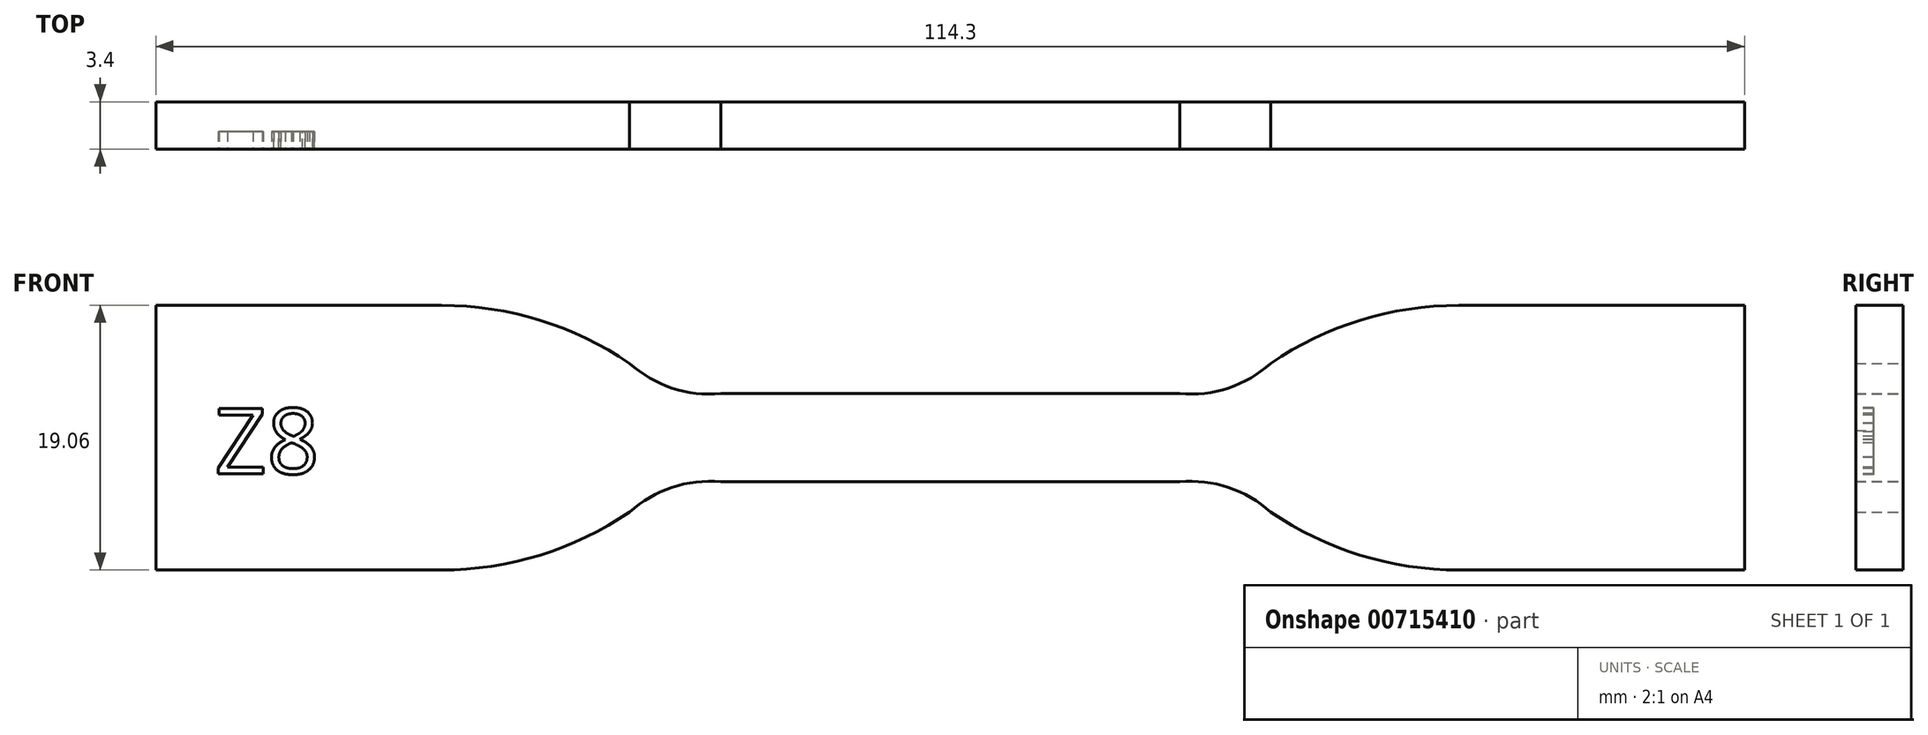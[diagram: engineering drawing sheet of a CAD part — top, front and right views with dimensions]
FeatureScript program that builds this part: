
annotation { "Feature Type Name" : "Feature", "Feature Type Description" : "" }
export const myFeature = defineFeature(function(context is Context, id is Id, definition is map)
    precondition{}
    {
        {
            var Q0;
            Q0=qCreatedBy(makeId("Front.planeOp"),FACE);
            var sketch = newSketch(context, id + "F0", { "sketchPlane" : qUnion([Q0])});
            skLineSegment(sketch, "E0", {"start": v(-57.15, 0) * mm, "end": v(-57.15, -9.52) * mm});
            skLineSegment(sketch, "E1", {"start": v(-57.15, -9.53) * mm, "end": v(-36.58, -9.53) * mm});
            skArc(sketch, "E2", {"start": v(-36.58, -9.53) * mm, "mid": v(-29.51, -8.46) * mm, "end": v(-23.07, -5.35) * mm});
            skArc(sketch, "E3", {"start": v(-16.51, -3.17) * mm, "mid": v(-20.02, -3.58) * mm, "end": v(-23.07, -5.35) * mm});
            skLineSegment(sketch, "E4", {"start": v(-16.51, -3.17) * mm, "end": v(0, -3.17) * mm});
            skArc(sketch, "E5.MirrorCS", {"start": v(-16.51, 3.17) * mm, "mid": v(-20.02, 3.58) * mm, "end": v(-23.07, 5.35) * mm});
            skLineSegment(sketch, "E6.MirrorCS", {"start": v(-16.51, 3.17) * mm, "end": v(0, 3.17) * mm});
            skArc(sketch, "E7.MirrorCS", {"start": v(-36.58, 9.53) * mm, "mid": v(-29.51, 8.46) * mm, "end": v(-23.07, 5.35) * mm});
            skLineSegment(sketch, "E8.MirrorCS", {"start": v(-57.15, 0) * mm, "end": v(-57.15, 9.52) * mm});
            skLineSegment(sketch, "E9.MirrorCS", {"start": v(-57.15, 9.53) * mm, "end": v(-36.58, 9.53) * mm});
            skArc(sketch, "E10.MirrorCS", {"start": v(36.58, -9.53) * mm, "mid": v(29.51, -8.46) * mm, "end": v(23.07, -5.35) * mm});
            skLineSegment(sketch, "E11.MirrorCS", {"start": v(57.15, 0) * mm, "end": v(57.15, -9.52) * mm});
            skArc(sketch, "E12.MirrorCS", {"start": v(16.51, -3.17) * mm, "mid": v(20.02, -3.58) * mm, "end": v(23.07, -5.35) * mm});
            skLineSegment(sketch, "E13.MirrorCS", {"start": v(16.51, 3.17) * mm, "end": v(0, 3.17) * mm});
            skLineSegment(sketch, "E14.MirrorCS", {"start": v(57.15, -9.53) * mm, "end": v(36.58, -9.53) * mm});
            skArc(sketch, "E15.MirrorCS", {"start": v(16.51, 3.17) * mm, "mid": v(20.02, 3.58) * mm, "end": v(23.07, 5.35) * mm});
            skArc(sketch, "E16.MirrorCS", {"start": v(36.58, 9.53) * mm, "mid": v(29.51, 8.46) * mm, "end": v(23.07, 5.35) * mm});
            skLineSegment(sketch, "E17.MirrorCS", {"start": v(57.15, 9.53) * mm, "end": v(36.58, 9.53) * mm});
            skLineSegment(sketch, "E18.MirrorCS", {"start": v(57.15, 0) * mm, "end": v(57.15, 9.52) * mm});
            skLineSegment(sketch, "E19.MirrorCS", {"start": v(16.51, -3.17) * mm, "end": v(0, -3.17) * mm});
            skSolve(sketch);
        }
        {
            var Q0;
            Q0=qSketchRegion(id+"F0",true);
            extrude(context, id + "F1", {"entities" : qUnion([Q0]), "depth" : 3.4 * mm, "offsetDistance" : 25.4 * mm});
        }
        {
            var Q0;
            Q0=makeQuery(id+"F1.opExtrude","CAP_FACE",FACE,{"disambiguationData":[OSD([sQuery(id+"F0.wireOp",EDGE,"E0"),sQuery(id+"F0.wireOp",EDGE,"E1"),sQuery(id+"F0.wireOp",EDGE,"E2"),sQuery(id+"F0.wireOp",EDGE,"E3"),sQuery(id+"F0.wireOp",EDGE,"E4"),sQuery(id+"F0.wireOp",EDGE,"E5.MirrorCS"),sQuery(id+"F0.wireOp",EDGE,"E6.MirrorCS"),sQuery(id+"F0.wireOp",EDGE,"E7.MirrorCS"),sQuery(id+"F0.wireOp",EDGE,"E8.MirrorCS"),sQuery(id+"F0.wireOp",EDGE,"E9.MirrorCS"),sQuery(id+"F0.wireOp",EDGE,"E10.MirrorCS"),sQuery(id+"F0.wireOp",EDGE,"E11.MirrorCS"),sQuery(id+"F0.wireOp",EDGE,"E12.MirrorCS"),sQuery(id+"F0.wireOp",EDGE,"E13.MirrorCS"),sQuery(id+"F0.wireOp",EDGE,"E14.MirrorCS"),sQuery(id+"F0.wireOp",EDGE,"E15.MirrorCS"),sQuery(id+"F0.wireOp",EDGE,"E16.MirrorCS"),sQuery(id+"F0.wireOp",EDGE,"E17.MirrorCS"),sQuery(id+"F0.wireOp",EDGE,"E18.MirrorCS"),sQuery(id+"F0.wireOp",EDGE,"E19.MirrorCS")])],"isStart":false});
            var sketch = newSketch(context, id + "F2", { "sketchPlane" : qUnion([Q0])});
            skText(sketch, "E20", { "text": "Z8", "fontName": "OpenSans-Regular.ttf"});
            const initialGuessF2  = {"E20": [-0.05293, -0.0026, 1, 0, 0.00475]};
            skSetInitialGuess(sketch, initialGuessF2);
            skSolve(sketch);
        }
        {
            var Q0;
            Q0 = qSketchRegion(id + "F2", true);
            extrude(context, id + "F3", {"entities" : qUnion([Q0]), "operationType" : NewBodyOperationType.REMOVE, "oppositeDirection" : true, "depth" : 1.27 * mm, "offsetDistance" : 25.4 * mm});
        }
    });
